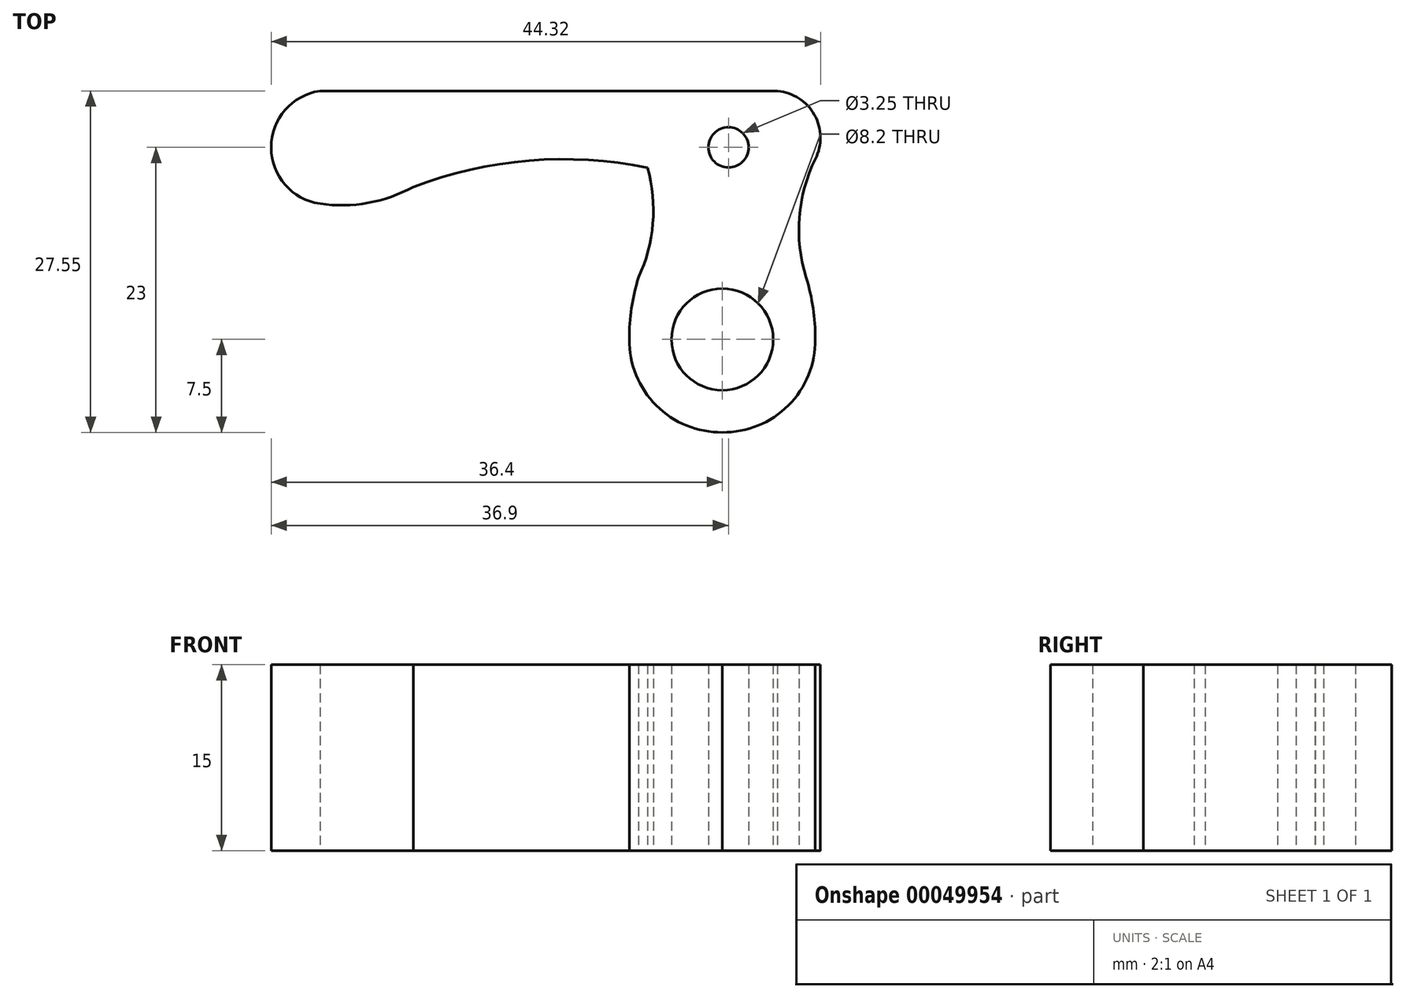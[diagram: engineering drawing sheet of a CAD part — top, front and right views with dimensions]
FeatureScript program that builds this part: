
annotation { "Feature Type Name" : "Feature", "Feature Type Description" : "" }
export const myFeature = defineFeature(function(context is Context, id is Id, definition is map)
    precondition{}
    {
        {
            var Q0;
            Q0=qCreatedBy(makeId("Top.planeOp"),FACE);
            var sketch = newSketch(context, id + "F0", { "sketchPlane" : qUnion([Q0])});
            skPoint(sketch, "E0.rect.middle", {"position": v(0, 0) * mm});
            skCircle(sketch, "E1", {"center": v(15.5, 15.5) * mm, "radius": 1.63 * mm});
            skLineSegment(sketch, "E2.rect.bottom", {"start": v(15.5, 15.5) * mm, "end": v(-15.5, 15.5) * mm, "construction": true});
            skLineSegment(sketch, "E2.rect.top", {"start": v(15.5, -15.5) * mm, "end": v(-15.5, -15.5) * mm, "construction": true});
            skLineSegment(sketch, "E2.rect.left", {"start": v(15.5, 15.5) * mm, "end": v(15.5, -15.5) * mm, "construction": true});
            skLineSegment(sketch, "E2.rect.right", {"start": v(-15.5, 15.5) * mm, "end": v(-15.5, -15.5) * mm, "construction": true});
            skCircle(sketch, "E3.0.1.0", {"center": v(15.5, -15.5) * mm, "radius": 1.63 * mm});
            skCircle(sketch, "E3.1.1.0", {"center": v(-15.5, -15.5) * mm, "radius": 1.63 * mm});
            skCircle(sketch, "E4", {"center": v(0, 0) * mm, "radius": 4 * mm, "construction": true});
            skLineSegment(sketch, "E5", {"start": v(0, 0) * mm, "end": v(15, 0) * mm, "construction": true});
            skPoint(sketch, "E5.endSnap0", {"position": v(15.5, 0) * mm});
            skCircle(sketch, "E6", {"center": v(15, 0) * mm, "radius": 11 * mm, "construction": true});
            skCircle(sketch, "E7", {"center": v(15, 0) * mm, "radius": 4.1 * mm});
            skArc(sketch, "E8", {"start": v(-17.46, 20.05) * mm, "mid": v(-21.4, 15.5) * mm, "end": v(-17.46, 10.95) * mm});
            skArc(sketch, "E9", {"start": v(-17.46, 10.95) * mm, "mid": v(-13.58, 11.02) * mm, "end": v(-9.93, 12.3) * mm});
            skArc(sketch, "E10", {"start": v(8.98, 13.85) * mm, "mid": v(-0.58, 14.43) * mm, "end": v(-9.93, 12.3) * mm});
            skArc(sketch, "E11", {"start": v(8.24, 5) * mm, "mid": v(9.4, 9.36) * mm, "end": v(8.98, 13.85) * mm});
            skLineSegment(sketch, "E12", {"start": v(-17.46, 20.05) * mm, "end": v(19.45, 20.05) * mm});
            skArc(sketch, "E13", {"start": v(22.51, 14.57) * mm, "mid": v(22.43, 18.12) * mm, "end": v(19.45, 20.05) * mm});
            skLineSegment(sketch, "E14", {"start": v(15, 0) * mm, "end": v(15, -7.5) * mm, "construction": true});
            skArc(sketch, "E15", {"start": v(7.5, 0) * mm, "mid": v(9.67, -5.33) * mm, "end": v(15, -7.5) * mm});
            skArc(sketch, "E16", {"start": v(8.24, 5) * mm, "mid": v(7.67, 2.53) * mm, "end": v(7.5, 0) * mm});
            skArc(sketch, "E17.MirrorCS", {"start": v(22.5, 0) * mm, "mid": v(20.33, -5.33) * mm, "end": v(15, -7.5) * mm});
            skArc(sketch, "E18.MirrorCS", {"start": v(21.76, 5) * mm, "mid": v(22.33, 2.53) * mm, "end": v(22.5, 0) * mm});
            skArc(sketch, "E19", {"start": v(22.51, 14.57) * mm, "mid": v(21.22, 9.86) * mm, "end": v(21.76, 5) * mm});
            skSolve(sketch);
        }
        {
            var Q0;
            Q0=makeQuery(id+"F0.imprint","IMPRINT",FACE,{"disambiguationData":[TD([[makeQuery(id+"F0.imprint","IMPRINT",EDGE,{"derivedFrom":sQuery(id+"F0.wireOp",EDGE,"E1")}),-1.0]])]});
            extrude(context, id + "F1", {"entities" : qUnion([Q0]), "depth" : 15 * mm});
        }
    });
